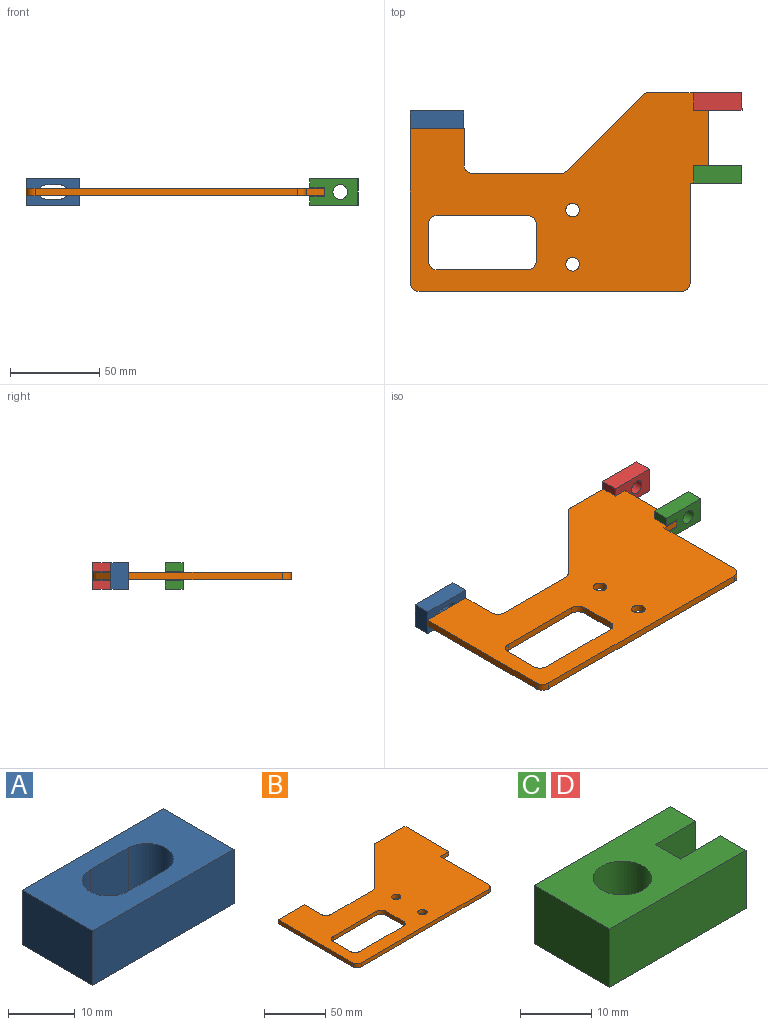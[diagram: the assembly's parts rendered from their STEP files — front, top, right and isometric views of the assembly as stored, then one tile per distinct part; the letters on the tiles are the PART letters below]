
ASSEMBLY  parts=4 mates=3
PART A: 10 faces, bbox 30x15x10 mm
  f0: plane 30x10mm, normal (0,-1,0), area 300mm2, adj f1,f7,f8,f9
  f1: plane 15x10mm, normal (1,0,0), area 150mm2, adj f0,f2,f8,f9
  f2: plane 30x10mm, normal (0,1,0), area 300mm2, adj f1,f7,f8,f9
  f3: cylinder r=4mm len=10mm, axis (0,0,-1), area 125.7mm2, adj f4,f6,f8,f9
  f4: plane 10x8mm, normal (0,-1,0), area 80mm2, adj f3,f5,f8,f9
  f5: cylinder r=4mm len=10mm, axis (0,0,-1), area 125.7mm2, adj f4,f6,f8,f9
  f6: plane 10x8mm, normal (0,1,0), area 80mm2, adj f3,f5,f8,f9
  f7: plane 15x10mm, normal (-1,0,0), area 150mm2, adj f0,f2,f8,f9
  f8: plane 30x15mm, normal (0,0,1), area 335.7mm2, adj f0,f1,f2,f3,f4,f5,f6,f7
  f9: plane 30x15mm, normal (0,0,-1), area 335.7mm2, adj f0,f1,f2,f3,f4,f5,f6,f7
PART B: 27 faces, bbox 167.4x111.6x4 mm
  f0: plane 86.23x4mm, normal (-1,0,0), area 344.9mm2, adj f1,f22,f25,f26
  f1: cylinder r=5.07mm len=5.07mm, axis (0,0,-1), area 31.9mm2, adj f0,f2,f25,f26
  f2: plane 147.1x4mm, normal (0,-1,0), area 588.4mm2, adj f1,f3,f25,f26
  f3: cylinder r=5.07mm len=5.07mm, axis (0,0,-1), area 31.9mm2, adj f2,f4,f25,f26
  f4: plane 55.73x4mm, normal (1,0,0), area 222.9mm2, adj f3,f5,f25,f26
  f5: plane 10.15x4mm, normal (0,-1,0), area 40.6mm2, adj f4,f6,f25,f26
  f6: plane 50.79x4mm, normal (1,0,0), area 203.1mm2, adj f5,f7,f25,f26
  f7: plane 33.41x4mm, normal (0,1,0), area 133.6mm2, adj f6,f8,f25,f26
  f8: cylinder r=5.07mm len=4mm, axis (0,0,-1), area 15.9mm2, adj f7,f9,f25,f26
  f9: plane 42.68x42.68mm, normal (-0.71,0.71,0), area 241.4mm2, adj f8,f10,f25,f26
  f10: cylinder r=5.07mm len=4mm, axis (0,0,-1), area 15.9mm2, adj f9,f11,f25,f26
  f11: plane 48.62x4mm, normal (0,1,0), area 194.5mm2, adj f10,f12,f25,f26
  f12: cylinder r=5.07mm len=5.07mm, axis (0,0,-1), area 31.9mm2, adj f11,f13,f25,f26
  f13: plane 20.29x4mm, normal (1,0,0), area 81.2mm2, adj f12,f22,f25,f26
  f14: cylinder r=5.07mm len=5.07mm, axis (0,0,-1), area 31.9mm2, adj f15,f23,f25,f26
  f15: plane 20.29x4mm, normal (-1,0,0), area 81.2mm2, adj f14,f16,f25,f26
  f16: cylinder r=5.07mm len=5.07mm, axis (0,0,-1), area 31.9mm2, adj f15,f17,f25,f26
  f17: plane 50.72x4mm, normal (0,1,0), area 202.9mm2, adj f16,f18,f25,f26
  f18: cylinder r=5.07mm len=5.07mm, axis (0,0,-1), area 31.9mm2, adj f17,f19,f25,f26
  f19: plane 20.29x4mm, normal (1,0,0), area 81.2mm2, adj f18,f20,f25,f26
  f20: cylinder r=5.07mm len=5.07mm, axis (0,0,-1), area 31.9mm2, adj f19,f23,f25,f26
  f21: cylinder r=3.8mm len=7.61mm, axis (0,0,-1), area 95.6mm2, adj f25,f26
  f22: plane 30.43x4mm, normal (0,1,0), area 121.7mm2, adj f0,f13,f25,f26
  f23: plane 50.72x4mm, normal (0,-1,0), area 202.9mm2, adj f14,f20,f25,f26
  f24: cylinder r=3.8mm len=7.61mm, axis (0,0,-1), area 95.6mm2, adj f25,f26
  f25: plane 167.39x111.59mm, normal (0,0,1), area 11928.3mm2, adj f0,f1,f2,f3,f4,f5,f6,f7
  f26: plane 167.39x111.59mm, normal (0,0,-1), area 11928.3mm2, adj f0,f1,f2,f3,f4,f5,f6,f7
PART C: 11 faces, bbox 27x15x10 mm
  f0: plane 10x5mm, normal (1,0,0), area 50mm2, adj f1,f7,f9,f10
  f1: plane 27x10mm, normal (0,1,0), area 270mm2, adj f0,f2,f9,f10
  f2: plane 15x10mm, normal (-1,0,0), area 150mm2, adj f1,f3,f9,f10
  f3: plane 27x10mm, normal (0,-1,0), area 270mm2, adj f2,f4,f9,f10
  f4: plane 10x5mm, normal (1,0,0), area 50mm2, adj f3,f5,f9,f10
  f5: plane 10x8mm, normal (0,1,0), area 80mm2, adj f4,f6,f9,f10
  f6: plane 10x5mm, normal (1,0,0), area 50mm2, adj f5,f7,f9,f10
  f7: plane 10x8mm, normal (0,-1,0), area 80mm2, adj f0,f6,f9,f10
  f8: cylinder r=4.1mm len=10mm, axis (0,0,-1), area 257.6mm2, adj f9,f10
  f9: plane 27x15mm, normal (0,0,1), area 312.2mm2, adj f0,f1,f2,f3,f4,f5,f6,f7
  f10: plane 27x15mm, normal (0,0,-1), area 312.2mm2, adj f0,f1,f2,f3,f4,f5,f6,f7
PART D: same geometry as C
PLACE A rot(axis=(-1,0,0),90deg) t=(-82.22,37.38,14.74)mm
PLACE B t=(-22.3,-8.89,14.72)mm fixed
PLACE C rot(axis=(0,0.71,-0.71),180deg) t=(75.44,16.88,14.72)mm
PLACE D rot(axis=(0,0.71,-0.71),180deg) t=(75.44,57.67,14.72)mm
MATE fastened D.f6 <-> B.f6  axis (-1,0,0) through (69.94,52.67,14.72)mm
MATE fastened C.f6 <-> B.f6  axis (-1,0,0) through (69.94,11.88,14.72)mm
MATE fastened A.f9 <-> B.f22  axis (0,-1,0) through (-82.22,37.38,14.72)mm
